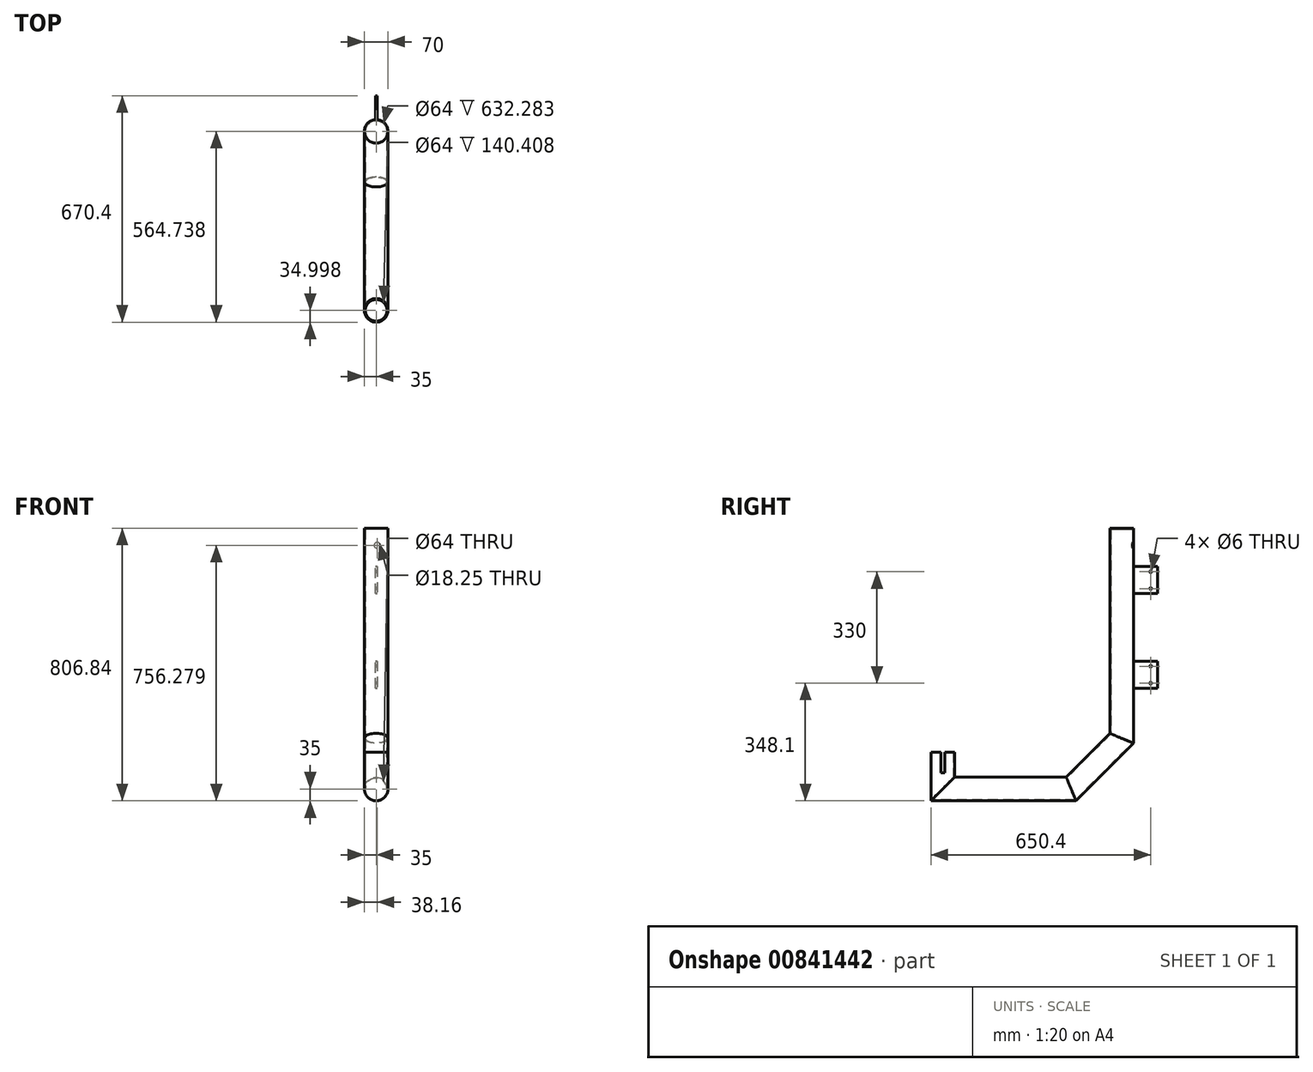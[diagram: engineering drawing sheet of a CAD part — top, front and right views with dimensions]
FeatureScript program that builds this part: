
annotation { "Feature Type Name" : "Feature", "Feature Type Description" : "" }
export const myFeature = defineFeature(function(context is Context, id is Id, definition is map)
    precondition{}
    {
        {
            var Q0;
            Q0=qCreatedBy(makeId("Right.planeOp"),FACE);
            var sketch = newSketch(context, id + "F0", { "sketchPlane" : qUnion([Q0])});
            skLineSegment(sketch, "E0", {"start": v(-15.66, 156.07) * mm, "end": v(-15.66, 763.54) * mm});
            skLineSegment(sketch, "E1", {"start": v(-145.04, 26.7) * mm, "end": v(-545.4, 26.7) * mm});
            skLineSegment(sketch, "E2", {"start": v(-15.66, 763.54) * mm, "end": v(54.34, 763.54) * mm});
            skLineSegment(sketch, "E3.0", {"start": v(54.34, 127.06) * mm, "end": v(54.34, 763.54) * mm});
            skLineSegment(sketch, "E3.2", {"start": v(-116.02, -43.3) * mm, "end": v(-545.4, -43.3) * mm});
            skLineSegment(sketch, "E4", {"start": v(-15.66, 156.07) * mm, "end": v(-145.04, 26.7) * mm});
            skLineSegment(sketch, "E5", {"start": v(54.34, 127.06) * mm, "end": v(-116.02, -43.3) * mm});
            skLineSegment(sketch, "E6", {"start": v(-545.4, 26.7) * mm, "end": v(-545.4, -43.3) * mm});
            skSolve(sketch);
        }
        {
            var Q0;
            Q0=makeQuery(id+"F0.imprint","IMPRINT",FACE,{"disambiguationData":[TD([[makeQuery(id+"F0.imprint","IMPRINT",EDGE,{"derivedFrom":sQuery(id+"F0.wireOp",EDGE,"E0")}),-1.0]])]});
            extrude(context, id + "F1", {"entities" : qUnion([Q0]), "depth" : 70 * mm, "offsetDistance" : 25.4 * mm});
        }
        {
            var Q0;
            Q0=qCreatedBy(makeId("Top.planeOp"),FACE);
            cPlane(context, id + "F2", {"entities" : qUnion([Q0]), "cplaneType" : CPlaneType.OFFSET, "offset" : 100 * mm, "width" : 152.4 * mm, "height" : 152.4 * mm});
        }
        {
            var Q0;
            Q0=qCreatedBy(id+"F2.planeOp",FACE);
            var sketch = newSketch(context, id + "F3", { "sketchPlane" : qUnion([Q0])});
            skPoint(sketch, "E7.0", {"position": v(38, -650) * mm});
            skLineSegment(sketch, "E8.0.0", {"start": v(0, -145.04) * mm, "end": v(0, -545.4) * mm});
            skLineSegment(sketch, "E8.0.1", {"start": v(0, -545.4) * mm, "end": v(70, -545.4) * mm});
            skLineSegment(sketch, "E8.0.2", {"start": v(70, -545.4) * mm, "end": v(70, -145.04) * mm});
            skLineSegment(sketch, "E8.0.3", {"start": v(70, -145.04) * mm, "end": v(0, -145.04) * mm});
            skLineSegment(sketch, "E9", {"start": v(0, -545.4) * mm, "end": v(0, -475.4) * mm});
            skLineSegment(sketch, "E10", {"start": v(0, -475.4) * mm, "end": v(70, -475.4) * mm});
            skLineSegment(sketch, "E11", {"start": v(70, -475.4) * mm, "end": v(0, -545.4) * mm});
            skLineSegment(sketch, "E12", {"start": v(0, -475.4) * mm, "end": v(70, -545.4) * mm});
            skCircle(sketch, "E13", {"center": v(35, -510.4) * mm, "radius": 35 * mm});
            skSolve(sketch);
        }
        {
            var Q0;
            Q0=qCreatedBy(makeId("Front.planeOp"),FACE);
            cPlane(context, id + "F4", {"entities" : qUnion([Q0]), "cplaneType" : CPlaneType.OFFSET, "offset" : 125 * mm, "oppositeDirection" : true, "width" : 152.4 * mm, "height" : 152.4 * mm});
        }
        {
            var Q0;
            Q0=qCreatedBy(id+"F4.planeOp",FACE);
            var sketch = newSketch(context, id + "F5", { "sketchPlane" : qUnion([Q0])});
            skLineSegment(sketch, "E14.0.0", {"start": v(37.9, 199.8) * mm, "end": v(-0.1, 199.8) * mm});
            skLineSegment(sketch, "E14.0.1", {"start": v(-0.1, 199.8) * mm, "end": v(-0.1, 799.8) * mm});
            skLineSegment(sketch, "E14.0.2", {"start": v(-0.1, 799.8) * mm, "end": v(37.9, 799.8) * mm});
            skLineSegment(sketch, "E14.0.3", {"start": v(37.9, 799.8) * mm, "end": v(37.9, 199.8) * mm});
            skLineSegment(sketch, "E15.0.0", {"start": v(75.9, 799.8) * mm, "end": v(75.9, 199.8) * mm});
            skLineSegment(sketch, "E15.0.1", {"start": v(75.9, 199.8) * mm, "end": v(37.9, 199.8) * mm});
            skLineSegment(sketch, "E15.0.2", {"start": v(37.9, 199.8) * mm, "end": v(37.9, 799.8) * mm});
            skLineSegment(sketch, "E15.0.3", {"start": v(37.9, 799.8) * mm, "end": v(75.9, 799.8) * mm});
            skLineSegment(sketch, "E16.bottom", {"start": v(37.9, 649.8) * mm, "end": v(32.9, 649.8) * mm});
            skLineSegment(sketch, "E16.top", {"start": v(37.9, 569.8) * mm, "end": v(32.9, 569.8) * mm});
            skLineSegment(sketch, "E16.left", {"start": v(37.9, 649.8) * mm, "end": v(37.9, 569.8) * mm});
            skLineSegment(sketch, "E16.right", {"start": v(32.9, 649.8) * mm, "end": v(32.9, 569.8) * mm});
            skLineSegment(sketch, "E17.bottom", {"start": v(37.9, 369.8) * mm, "end": v(33, 369.8) * mm});
            skLineSegment(sketch, "E17.top", {"start": v(37.9, 289.8) * mm, "end": v(33, 289.8) * mm});
            skLineSegment(sketch, "E17.left", {"start": v(37.9, 369.8) * mm, "end": v(37.9, 289.8) * mm});
            skLineSegment(sketch, "E17.right", {"start": v(33, 369.8) * mm, "end": v(33, 289.8) * mm});
            skSolve(sketch);
        }
        {
            var Q0;
            Q0=makeQuery(id+"F5.imprint","IMPRINT",FACE,{"disambiguationData":[TD([[makeQuery(id+"F5.imprint","IMPRINT",EDGE,{"derivedFrom":sQuery(id+"F5.wireOp",EDGE,"E16.bottom")}),1.0]])]});
            var Q1;
            Q1=makeQuery(id+"F5.imprint","IMPRINT",FACE,{"disambiguationData":[TD([[makeQuery(id+"F5.imprint","IMPRINT",EDGE,{"derivedFrom":sQuery(id+"F5.wireOp",EDGE,"E17.bottom")}),1.0]])]});
            extrude(context, id + "F6", {"entities" : qUnion([Q0, Q1]), "operationType" : NewBodyOperationType.ADD, "endBound" : BoundingType.UP_TO_NEXT, "depth" : 25.4 * mm, "offsetDistance" : 25.4 * mm});
        }
        {
            var Q0;
            Q0=makeQuery(id+"F6.opExtrude","SWEPT_FACE",FACE,{"disambiguationData":[OSD([sQuery(id+"F5.wireOp",EDGE,"E16.right")])]});
            var sketch = newSketch(context, id + "F7", { "sketchPlane" : qUnion([Q0])});
            skLineSegment(sketch, "E18.0.0", {"start": v(-125, 569.8) * mm, "end": v(-54.34, 569.8) * mm});
            skLineSegment(sketch, "E18.0.1", {"start": v(-54.34, 569.8) * mm, "end": v(-54.34, 649.8) * mm});
            skLineSegment(sketch, "E18.0.2", {"start": v(-54.34, 649.8) * mm, "end": v(-125, 649.8) * mm});
            skLineSegment(sketch, "E18.0.3", {"start": v(-125, 649.8) * mm, "end": v(-125, 569.8) * mm});
            skLineSegment(sketch, "E19.0.0", {"start": v(-125, 289.8) * mm, "end": v(-54.34, 289.8) * mm});
            skLineSegment(sketch, "E19.0.1", {"start": v(-54.34, 289.8) * mm, "end": v(-54.34, 369.8) * mm});
            skLineSegment(sketch, "E19.0.2", {"start": v(-54.34, 369.8) * mm, "end": v(-125, 369.8) * mm});
            skLineSegment(sketch, "E19.0.3", {"start": v(-125, 369.8) * mm, "end": v(-125, 289.8) * mm});
            skCircle(sketch, "E20", {"center": v(-105, 634.8) * mm, "radius": 3 * mm});
            skCircle(sketch, "E21", {"center": v(-105, 584.8) * mm, "radius": 3 * mm});
            skCircle(sketch, "E22", {"center": v(-105, 354.8) * mm, "radius": 3 * mm});
            skCircle(sketch, "E23", {"center": v(-105, 304.8) * mm, "radius": 3 * mm});
            skSolve(sketch);
        }
        {
            var Q0;
            Q0=makeQuery(id+"F7.imprint","IMPRINT",FACE,{"disambiguationData":[TD([[makeQuery(id+"F7.imprint","IMPRINT",EDGE,{"derivedFrom":sQuery(id+"F7.wireOp",EDGE,"E20")}),1.0]])]});
            var Q1;
            Q1=makeQuery(id+"F7.imprint","IMPRINT",FACE,{"disambiguationData":[TD([[makeQuery(id+"F7.imprint","IMPRINT",EDGE,{"derivedFrom":sQuery(id+"F7.wireOp",EDGE,"E21")}),1.0]])]});
            var Q2;
            Q2=makeQuery(id+"F7.imprint","IMPRINT",FACE,{"disambiguationData":[TD([[makeQuery(id+"F7.imprint","IMPRINT",EDGE,{"derivedFrom":sQuery(id+"F7.wireOp",EDGE,"E22")}),1.0]])]});
            var Q3;
            Q3=makeQuery(id+"F7.imprint","IMPRINT",FACE,{"disambiguationData":[TD([[makeQuery(id+"F7.imprint","IMPRINT",EDGE,{"derivedFrom":sQuery(id+"F7.wireOp",EDGE,"E23")}),1.0]])]});
            extrude(context, id + "F8", {"entities" : qUnion([Q0, Q1, Q2, Q3]), "operationType" : NewBodyOperationType.REMOVE, "oppositeDirection" : true, "depth" : 25.4 * mm, "offsetDistance" : 25.4 * mm});
        }
        {
            var Q0;
            Q0=qCreatedBy(makeId("Right.planeOp"),FACE);
            var sketch = newSketch(context, id + "F9", { "sketchPlane" : qUnion([Q0])});
            skLineSegment(sketch, "E24", {"start": v(-457, 100) * mm, "end": v(-457, -3.2) * mm});
            skLineSegment(sketch, "E25", {"start": v(-527, -3.2) * mm, "end": v(-527, 100) * mm});
            skLineSegment(sketch, "E26.0", {"start": v(-530, 100) * mm, "end": v(-454, 100) * mm});
            skLineSegment(sketch, "E27", {"start": v(-454, 100) * mm, "end": v(-441.92, 100) * mm});
            skLineSegment(sketch, "E28", {"start": v(-441.92, 100) * mm, "end": v(-441.92, 45) * mm});
            skLineSegment(sketch, "E29", {"start": v(-441.92, 45) * mm, "end": v(-549.12, 45) * mm});
            skLineSegment(sketch, "E30", {"start": v(-549.12, 45) * mm, "end": v(-549.12, 100) * mm});
            skLineSegment(sketch, "E31", {"start": v(-549.12, 100) * mm, "end": v(-441.92, 100) * mm});
            skCircle(sketch, "E32", {"center": v(-495.52, 45) * mm, "radius": 4.9 * mm});
            skSolve(sketch);
        }
        {
            var Q0;
            {var subQ0=sQuery(id+"F9.wireOp",EDGE,"E32");var subQ1=sQuery(id+"F9.wireOp",EDGE,"E29");var subQ2=makeQuery(id+"F9.imprint","INTERSECT",VERTEX,{"disambiguationData":[OD(0.0)],"derivedFrom":[subQ1,subQ0]});Q0=makeQuery(id+"F9.imprint","IMPRINT",FACE,{"disambiguationData":[TD([[makeQuery(id+"F9.imprint","IMPRINT",EDGE,{"disambiguationData":[TD([[subQ2,-1.0]])],"derivedFrom":subQ1}),1.0]])]});}
            var Q1;
            {var subQ0=sQuery(id+"F9.wireOp",EDGE,"E32");var subQ1=sQuery(id+"F9.wireOp",EDGE,"E29");var subQ2=makeQuery(id+"F9.imprint","INTERSECT",VERTEX,{"disambiguationData":[OD(0.0)],"derivedFrom":[subQ1,subQ0]});Q1=makeQuery(id+"F9.imprint","IMPRINT",FACE,{"disambiguationData":[TD([[makeQuery(id+"F9.imprint","IMPRINT",EDGE,{"disambiguationData":[TD([[subQ2,-1.0]])],"derivedFrom":subQ1}),-1.0]])]});}
            extrude(context, id + "F10", {"entities" : qUnion([Q0, Q1]), "operationType" : NewBodyOperationType.REMOVE, "endBound" : BoundingType.SYMMETRIC, "oppositeDirection" : true, "depth" : 239.78 * mm, "offsetDistance" : 25.4 * mm});
        }
        {
            var Q0;
            Q0=qCreatedBy(id+"F4.planeOp",FACE);
            var sketch = newSketch(context, id + "F11", { "sketchPlane" : qUnion([Q0])});
            skCircle(sketch, "E33", {"center": v(38.16, 712.98) * mm, "radius": 9.13 * mm});
            skSolve(sketch);
        }
        {
            var Q0;
            Q0=makeQuery(id+"F1.opExtrude","CAP_EDGE",EDGE,{"disambiguationData":[OSD([sQuery(id+"F0.wireOp",EDGE,"E0")])],"isStart":true});
            var Q1;
            Q1=makeQuery(id+"F1.opExtrude","CAP_EDGE",EDGE,{"disambiguationData":[OSD([sQuery(id+"F0.wireOp",EDGE,"E3.0")])],"isStart":true});
            var Q2;
            Q2=makeQuery(id+"F1.opExtrude","CAP_EDGE",EDGE,{"disambiguationData":[OSD([sQuery(id+"F0.wireOp",EDGE,"E4")])],"isStart":true});
            var Q3;
            Q3=makeQuery(id+"F1.opExtrude","CAP_EDGE",EDGE,{"disambiguationData":[OSD([sQuery(id+"F0.wireOp",EDGE,"E5")])],"isStart":true});
            var Q4;
            Q4=makeQuery(id+"F1.opExtrude","CAP_EDGE",EDGE,{"disambiguationData":[OSD([sQuery(id+"F0.wireOp",EDGE,"E1")])],"isStart":true});
            var Q5;
            Q5=makeQuery(id+"F1.opExtrude","CAP_EDGE",EDGE,{"disambiguationData":[OSD([sQuery(id+"F0.wireOp",EDGE,"E3.2")])],"isStart":true});
            var Q6;
            Q6=makeQuery(id+"F1.opExtrude","CAP_EDGE",EDGE,{"disambiguationData":[OSD([sQuery(id+"F0.wireOp",EDGE,"E1")])],"isStart":false});
            var Q7;
            Q7=makeQuery(id+"F1.opExtrude","CAP_EDGE",EDGE,{"disambiguationData":[OSD([sQuery(id+"F0.wireOp",EDGE,"E3.2")])],"isStart":false});
            var Q8;
            Q8=makeQuery(id+"F1.opExtrude","CAP_EDGE",EDGE,{"disambiguationData":[OSD([sQuery(id+"F0.wireOp",EDGE,"E5")])],"isStart":false});
            var Q9;
            Q9=makeQuery(id+"F1.opExtrude","CAP_EDGE",EDGE,{"disambiguationData":[OSD([sQuery(id+"F0.wireOp",EDGE,"E4")])],"isStart":false});
            var Q10;
            Q10=makeQuery(id+"F1.opExtrude","CAP_EDGE",EDGE,{"disambiguationData":[OSD([sQuery(id+"F0.wireOp",EDGE,"E0")])],"isStart":false});
            var Q11;
            Q11=makeQuery(id+"F1.opExtrude","CAP_EDGE",EDGE,{"disambiguationData":[OSD([sQuery(id+"F0.wireOp",EDGE,"E3.0")])],"isStart":false});
            fillet(context, id + "F12", {"entities" : qUnion([Q0, Q1, Q2, Q3, Q4, Q5, Q6, Q7, Q8, Q9, Q10, Q11]), "radius" : 35 * mm, "tangentPropagation" : true, "allowEdgeOverflow" : false});
        }
        {
            var Q0;
            Q0=qCreatedBy(makeId("Right.planeOp"),FACE);
            var sketch = newSketch(context, id + "F13", { "sketchPlane" : qUnion([Q0])});
            skLineSegment(sketch, "E34", {"start": v(-545.4, 26.7) * mm, "end": v(-145.04, 26.7) * mm});
            skLineSegment(sketch, "E35", {"start": v(-116.02, -43.3) * mm, "end": v(-545.4, -43.3) * mm});
            skPoint(sketch, "E36.0", {"position": v(-475.4, 100) * mm});
            skLineSegment(sketch, "E37", {"start": v(-475.4, 76.46) * mm, "end": v(-475.4, 26.7) * mm});
            skLineSegment(sketch, "E38", {"start": v(-475.4, 26.7) * mm, "end": v(-545.4, -43.3) * mm});
            skLineSegment(sketch, "E39", {"start": v(-570.18, -43.3) * mm, "end": v(-570.18, 76.46) * mm});
            skLineSegment(sketch, "E40", {"start": v(-570.18, 76.46) * mm, "end": v(-475.4, 76.46) * mm});
            skLineSegment(sketch, "E41", {"start": v(-545.4, -43.3) * mm, "end": v(-570.18, -43.3) * mm});
            skSolve(sketch);
        }
        {
            var Q0;
            Q0=makeQuery(id+"F13.imprint","IMPRINT",FACE,{"disambiguationData":[TD([[makeQuery(id+"F13.imprint","IMPRINT",EDGE,{"derivedFrom":sQuery(id+"F13.wireOp",EDGE,"E37")}),-1.0]])]});
            extrude(context, id + "F14", {"entities" : qUnion([Q0]), "operationType" : NewBodyOperationType.REMOVE, "depth" : 101.35 * mm, "offsetDistance" : 25.4 * mm});
        }
        {
            var Q0;
            {var subQ0=sQuery(id+"F3.wireOp",EDGE,"E12");var subQ1=sQuery(id+"F3.wireOp",EDGE,"E11");var subQ2=makeQuery(id+"F3.imprint","INTERSECT",VERTEX,{"derivedFrom":[subQ1,subQ0]});Q0=makeQuery(id+"F3.imprint","IMPRINT",FACE,{"disambiguationData":[TD([[makeQuery(id+"F3.imprint","IMPRINT",EDGE,{"disambiguationData":[TD([[subQ2,-1.0]])],"derivedFrom":subQ1}),1.0]])]});}
            var Q1;
            {var subQ0=sQuery(id+"F3.wireOp",EDGE,"E13");var subQ1=sQuery(id+"F3.wireOp",EDGE,"E11");var subQ2=makeQuery(id+"F3.imprint","INTERSECT",VERTEX,{"disambiguationData":[OD(0.0)],"derivedFrom":[subQ1,subQ0]});Q1=makeQuery(id+"F3.imprint","IMPRINT",FACE,{"disambiguationData":[TD([[makeQuery(id+"F3.imprint","IMPRINT",EDGE,{"disambiguationData":[TD([[subQ2,-1.0]])],"derivedFrom":subQ1}),-1.0]])]});}
            var Q2;
            {var subQ0=sQuery(id+"F3.wireOp",EDGE,"E12");var subQ1=sQuery(id+"F3.wireOp",EDGE,"E11");var subQ2=makeQuery(id+"F3.imprint","INTERSECT",VERTEX,{"derivedFrom":[subQ1,subQ0]});Q2=makeQuery(id+"F3.imprint","IMPRINT",FACE,{"disambiguationData":[TD([[makeQuery(id+"F3.imprint","IMPRINT",EDGE,{"disambiguationData":[TD([[subQ2,-1.0]])],"derivedFrom":subQ1}),-1.0]])]});}
            var Q3;
            {var subQ0=sQuery(id+"F3.wireOp",EDGE,"E13");var subQ1=sQuery(id+"F3.wireOp",EDGE,"E11");var subQ2=makeQuery(id+"F3.imprint","INTERSECT",VERTEX,{"disambiguationData":[OD(0.0)],"derivedFrom":[subQ1,subQ0]});Q3=makeQuery(id+"F3.imprint","IMPRINT",FACE,{"disambiguationData":[TD([[makeQuery(id+"F3.imprint","IMPRINT",EDGE,{"disambiguationData":[TD([[subQ2,-1.0]])],"derivedFrom":subQ1}),1.0]])]});}
            extrude(context, id + "F15", {"entities" : qUnion([Q0, Q1, Q2, Q3]), "operationType" : NewBodyOperationType.ADD, "endBound" : BoundingType.UP_TO_NEXT, "oppositeDirection" : true, "depth" : 25.4 * mm, "offsetDistance" : 25.4 * mm});
        }
        {
            var Q0;
            Q0=makeQuery(id+"F15.opExtrude","CAP_FACE",FACE,{"disambiguationData":[OSD([sQuery(id+"F3.wireOp",EDGE,"E13")])],"isStart":true});
            shell(context, id + "F16", {"entities" : qUnion([Q0]), "thickness" : 3 * mm});
        }
        {
            var Q0;
            Q0=makeQuery(id+"F11.imprint","IMPRINT",FACE,{"disambiguationData":[TD([[makeQuery(id+"F11.imprint","IMPRINT",EDGE,{"derivedFrom":sQuery(id+"F11.wireOp",EDGE,"E33")}),1.0]])]});
            extrude(context, id + "F17", {"entities" : qUnion([Q0]), "operationType" : NewBodyOperationType.REMOVE, "depth" : 102.62 * mm, "offsetDistance" : 25.4 * mm});
        }
        {
            var Q0;
            Q0=qCreatedBy(makeId("Right.planeOp"),FACE);
            var sketch = newSketch(context, id + "F18", { "sketchPlane" : qUnion([Q0])});
            skLineSegment(sketch, "E42", {"start": v(-475.4, 100) * mm, "end": v(-475.4, 26.7) * mm});
            skLineSegment(sketch, "E43", {"start": v(-545.4, -43.3) * mm, "end": v(-545.4, 100) * mm});
            skLineSegment(sketch, "E44.0", {"start": v(-545.4, 100) * mm, "end": v(-475.4, 100) * mm});
            skLineSegment(sketch, "E45", {"start": v(-475.4, 100) * mm, "end": v(-475.4, 120.98) * mm});
            skLineSegment(sketch, "E46", {"start": v(-475.4, 120.98) * mm, "end": v(-545.4, 120.98) * mm});
            skLineSegment(sketch, "E47", {"start": v(-545.4, 120.98) * mm, "end": v(-545.4, 100) * mm});
            skLineSegment(sketch, "E48", {"start": v(-475.4, 100) * mm, "end": v(-545.4, 100) * mm});
            skLineSegment(sketch, "E49", {"start": v(-510.4, 100) * mm, "end": v(-510.4, 40) * mm});
            skLineSegment(sketch, "E50", {"start": v(-510.4, 40) * mm, "end": v(-516.4, 40) * mm});
            skLineSegment(sketch, "E51", {"start": v(-516.4, 40) * mm, "end": v(-516.4, 100) * mm});
            skLineSegment(sketch, "E52", {"start": v(-516.4, 100) * mm, "end": v(-516.4, 108.85) * mm});
            skLineSegment(sketch, "E53", {"start": v(-516.4, 108.85) * mm, "end": v(-504.4, 108.85) * mm});
            skLineSegment(sketch, "E54", {"start": v(-504.4, 108.85) * mm, "end": v(-504.4, 40) * mm});
            skLineSegment(sketch, "E55", {"start": v(-504.4, 40) * mm, "end": v(-510.4, 40) * mm});
            skSolve(sketch);
        }
        {
            var Q0;
            {var subQ0=sQuery(id+"F18.wireOp",EDGE,"E49");Q0=makeQuery(id+"F18.imprint","IMPRINT",FACE,{"disambiguationData":[TD([[makeQuery(id+"F18.imprint","IMPRINT",EDGE,{"derivedFrom":subQ0}),1.0]])]});}
            var Q1;
            {var subQ0=sQuery(id+"F18.wireOp",EDGE,"3aLA14ol-1fBa-uuaq-JjUp-dM2QRVu7OhE4");Q1=makeQuery(id+"F18.imprint","IMPRINT",FACE,{"disambiguationData":[TD([[makeQuery(id+"F18.imprint","IMPRINT",EDGE,{"derivedFrom":subQ0}),-1.0]])]});}
            var Q2;
            {var subQ0=sQuery(id+"F18.wireOp",EDGE,"E49");Q2=makeQuery(id+"F18.imprint","IMPRINT",FACE,{"disambiguationData":[TD([[makeQuery(id+"F18.imprint","IMPRINT",EDGE,{"derivedFrom":subQ0}),-1.0]])]});}
            extrude(context, id + "F19", {"entities" : qUnion([Q0, Q1, Q2]), "operationType" : NewBodyOperationType.REMOVE, "depth" : 127.5 * mm, "offsetDistance" : 25.4 * mm});
        }
    });
